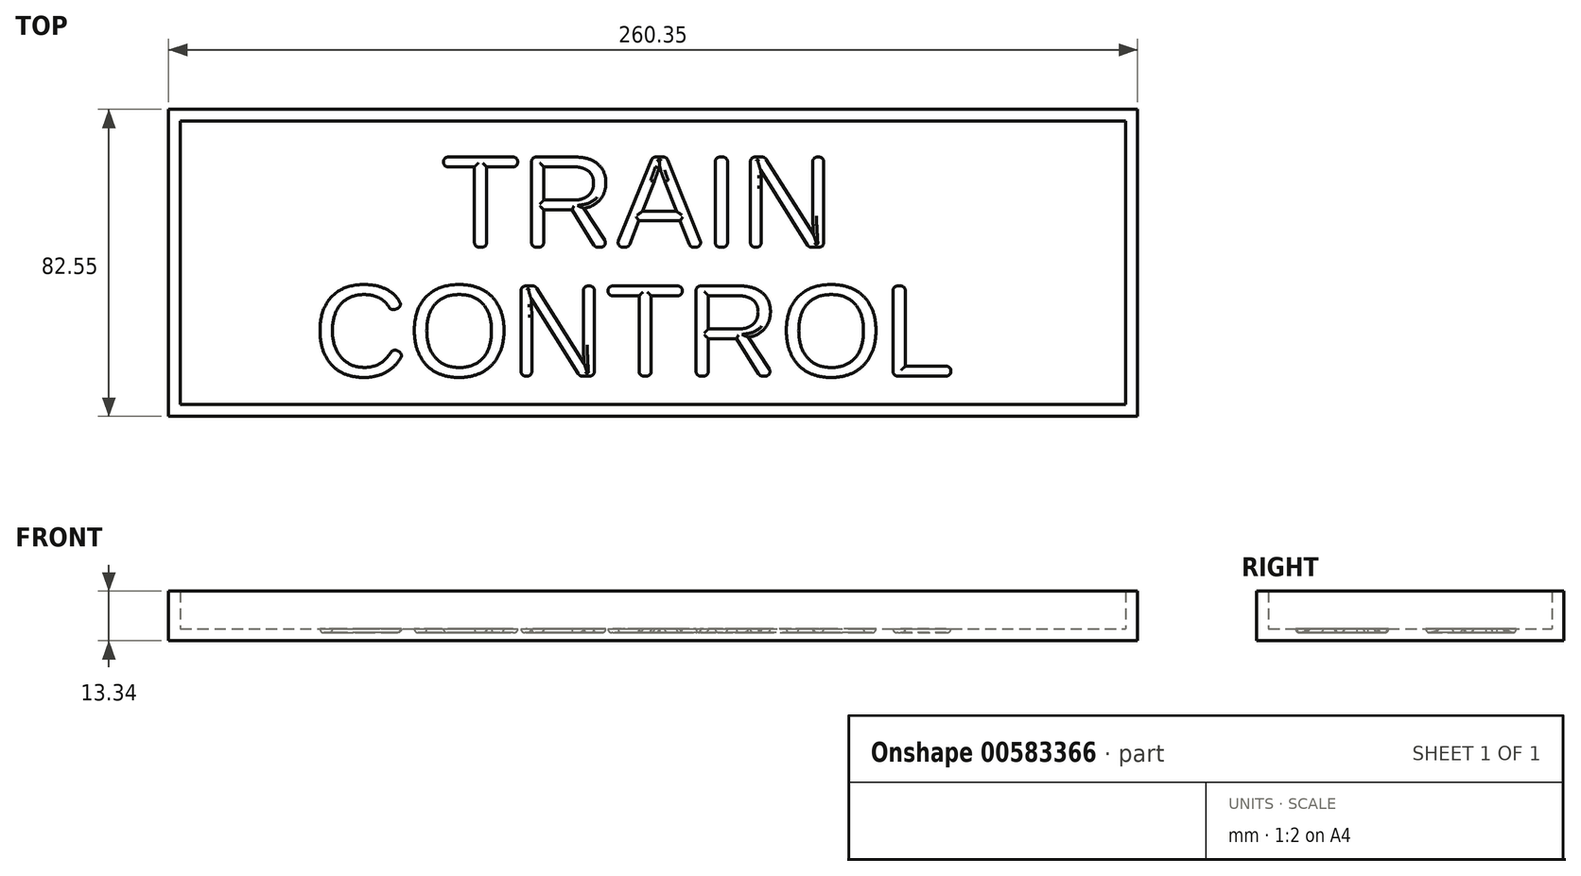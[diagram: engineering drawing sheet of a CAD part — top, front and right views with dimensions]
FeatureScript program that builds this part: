
annotation { "Feature Type Name" : "Feature", "Feature Type Description" : "" }
export const myFeature = defineFeature(function(context is Context, id is Id, definition is map)
    precondition{}
    {
        {
            var Q0;
            Q0=qCreatedBy(makeId("Top.planeOp"),FACE);
            var sketch = newSketch(context, id + "F0", { "sketchPlane" : qUnion([Q0])});
            skLineSegment(sketch, "E0.bottom", {"start": v(-122.6, -37.62) * mm, "end": v(131.4, -37.62) * mm});
            skLineSegment(sketch, "E0.top", {"start": v(-122.6, 38.58) * mm, "end": v(131.4, 38.58) * mm});
            skLineSegment(sketch, "E0.left", {"start": v(-122.6, -37.62) * mm, "end": v(-122.6, 38.58) * mm});
            skLineSegment(sketch, "E0.right", {"start": v(131.4, -37.62) * mm, "end": v(131.4, 38.58) * mm});
            skLineSegment(sketch, "E1.0", {"start": v(-125.77, 41.75) * mm, "end": v(134.58, 41.75) * mm});
            skLineSegment(sketch, "E1.1", {"start": v(-125.77, -40.8) * mm, "end": v(-125.77, 41.75) * mm});
            skLineSegment(sketch, "E1.2", {"start": v(-125.77, -40.8) * mm, "end": v(134.58, -40.8) * mm});
            skLineSegment(sketch, "E1.3", {"start": v(134.58, -40.8) * mm, "end": v(134.58, 41.75) * mm});
            skSolve(sketch);
        }
        {
            var Q0;
            Q0 = qSketchRegion(id + "F0", true);
            extrude(context, id + "F1", {"entities" : qUnion([Q0]), "depth" : 10.16 * mm, "offsetDistance" : 25.4 * mm});
        }
        {
            var Q0;
            Q0=qCreatedBy(makeId("Top.planeOp"),FACE);
            var sketch = newSketch(context, id + "F2", { "sketchPlane" : qUnion([Q0])});
            skLineSegment(sketch, "E2.0", {"start": v(-125.77, -40.8) * mm, "end": v(-125.77, 41.75) * mm});
            skLineSegment(sketch, "E2.1.0", {"start": v(134.58, -40.8) * mm, "end": v(-125.77, -40.8) * mm});
            skLineSegment(sketch, "E2.1.1", {"start": v(-125.77, -40.8) * mm, "end": v(-125.77, 41.75) * mm});
            skLineSegment(sketch, "E2.1.2", {"start": v(-125.77, 41.75) * mm, "end": v(134.58, 41.75) * mm});
            skLineSegment(sketch, "E2.1.3", {"start": v(134.58, 41.75) * mm, "end": v(134.58, -40.8) * mm});
            skSolve(sketch);
        }
        {
            var Q0;
            Q0 = qSketchRegion(id + "F2", true);
            extrude(context, id + "F3", {"entities" : qUnion([Q0]), "operationType" : NewBodyOperationType.ADD, "oppositeDirection" : true, "depth" : 3.17 * mm, "offsetDistance" : 25.4 * mm});
        }
        {
            var Q0;
            Q0=makeQuery(id+"F3.opExtrude","CAP_FACE",FACE,{"disambiguationData":[OSD([sQuery(id+"F2.wireOp",EDGE,"E2.1.0"),sQuery(id+"F2.wireOp",EDGE,"E2.1.1"),sQuery(id+"F2.wireOp",EDGE,"E2.1.2"),sQuery(id+"F2.wireOp",EDGE,"E2.1.3")])],"isStart":true});
            var sketch = newSketch(context, id + "F4", { "sketchPlane" : qUnion([Q0])});
            skText(sketch, "E3", { "text": "TRAIN", "fontName": "Arimo-Regular.ttf"});
            skText(sketch, "E4", { "text": "CONTROL", "fontName": "Arimo-Regular.ttf"});
            const initialGuessF4  = {"E3": [-0.0527, 0.00468, 1, 0, 0.0254], "E4": [-0.08688, -0.02998, 1, 0, 0.0254]};
            skSetInitialGuess(sketch, initialGuessF4);
            skSolve(sketch);
        }
        {
            var Q0;
            Q0 = qSketchRegion(id + "F4", true);
            extrude(context, id + "F5", {"entities" : qUnion([Q0]), "operationType" : NewBodyOperationType.REMOVE, "oppositeDirection" : true, "depth" : 1.02 * mm, "offsetDistance" : 25.4 * mm});
        }
        {
            var Q0;
            Q0=makeQuery(id+"F5.boolean.opBoolean","COPY",EDGE,{"derivedFrom":makeQuery(id+"F5.opExtrude","SWEPT_EDGE",EDGE,{"disambiguationData":[OSD([sQuery(id+"F4.wireOp",EDGE,"E3.sketch_text.stroke-4"),sQuery(id+"F4.wireOp",EDGE,"E3.sketch_text.stroke-5")])]})});
            var Q1;
            Q1=makeQuery(id+"F5.boolean.opBoolean","COPY",EDGE,{"derivedFrom":makeQuery(id+"F5.opExtrude","SWEPT_EDGE",EDGE,{"disambiguationData":[OSD([sQuery(id+"F4.wireOp",EDGE,"E3.sketch_text.stroke-5"),sQuery(id+"F4.wireOp",EDGE,"E3.sketch_text.stroke-6")])]})});
            var Q2;
            Q2=makeQuery(id+"F5.boolean.opBoolean","COPY",EDGE,{"derivedFrom":makeQuery(id+"F5.opExtrude","SWEPT_EDGE",EDGE,{"disambiguationData":[OSD([sQuery(id+"F4.wireOp",EDGE,"E3.sketch_text.stroke-6"),sQuery(id+"F4.wireOp",EDGE,"E3.sketch_text.stroke-7")])]})});
            var Q3;
            Q3=makeQuery(id+"F5.boolean.opBoolean","COPY",EDGE,{"derivedFrom":makeQuery(id+"F5.opExtrude","SWEPT_EDGE",EDGE,{"disambiguationData":[OSD([sQuery(id+"F4.wireOp",EDGE,"E3.sketch_text.stroke-3"),sQuery(id+"F4.wireOp",EDGE,"E3.sketch_text.stroke-4")])]})});
            var Q4;
            Q4=makeQuery(id+"F5.boolean.opBoolean","COPY",EDGE,{"derivedFrom":makeQuery(id+"F5.opExtrude","SWEPT_EDGE",EDGE,{"disambiguationData":[OSD([sQuery(id+"F4.wireOp",EDGE,"E3.sketch_text.stroke-1"),sQuery(id+"F4.wireOp",EDGE,"E3.sketch_text.stroke-2")])]})});
            var Q5;
            Q5=makeQuery(id+"F5.boolean.opBoolean","COPY",EDGE,{"derivedFrom":makeQuery(id+"F5.opExtrude","SWEPT_EDGE",EDGE,{"disambiguationData":[OSD([sQuery(id+"F4.wireOp",EDGE,"E3.sketch_text.stroke-11"),sQuery(id+"F4.wireOp",EDGE,"E3.sketch_text.stroke-12")])]})});
            var Q6;
            Q6=makeQuery(id+"F5.boolean.opBoolean","COPY",EDGE,{"derivedFrom":makeQuery(id+"F5.opExtrude","SWEPT_EDGE",EDGE,{"disambiguationData":[OSD([sQuery(id+"F4.wireOp",EDGE,"E3.sketch_text.stroke-8"),sQuery(id+"F4.wireOp",EDGE,"E3.sketch_text.stroke-19")])]})});
            var Q7;
            Q7=makeQuery(id+"F5.boolean.opBoolean","COPY",EDGE,{"derivedFrom":makeQuery(id+"F5.opExtrude","SWEPT_EDGE",EDGE,{"disambiguationData":[OSD([sQuery(id+"F4.wireOp",EDGE,"E3.sketch_text.stroke-30"),sQuery(id+"F4.wireOp",EDGE,"E3.sketch_text.stroke-31")])]})});
            var Q8;
            Q8=makeQuery(id+"F5.boolean.opBoolean","COPY",EDGE,{"derivedFrom":makeQuery(id+"F5.opExtrude","SWEPT_EDGE",EDGE,{"disambiguationData":[OSD([sQuery(id+"F4.wireOp",EDGE,"E3.sketch_text.stroke-27"),sQuery(id+"F4.wireOp",EDGE,"E3.sketch_text.stroke-34")])]})});
            var Q9;
            Q9=makeQuery(id+"F5.boolean.opBoolean","COPY",EDGE,{"derivedFrom":makeQuery(id+"F5.opExtrude","SWEPT_EDGE",EDGE,{"disambiguationData":[OSD([sQuery(id+"F4.wireOp",EDGE,"E3.sketch_text.stroke-42"),sQuery(id+"F4.wireOp",EDGE,"E3.sketch_text.stroke-45")])]})});
            var Q10;
            Q10=makeQuery(id+"F5.boolean.opBoolean","COPY",EDGE,{"derivedFrom":makeQuery(id+"F5.opExtrude","SWEPT_EDGE",EDGE,{"disambiguationData":[OSD([sQuery(id+"F4.wireOp",EDGE,"E3.sketch_text.stroke-50"),sQuery(id+"F4.wireOp",EDGE,"E3.sketch_text.stroke-51")])]})});
            var Q11;
            Q11=makeQuery(id+"F5.boolean.opBoolean","COPY",EDGE,{"derivedFrom":makeQuery(id+"F5.opExtrude","SWEPT_EDGE",EDGE,{"disambiguationData":[OSD([sQuery(id+"F4.wireOp",EDGE,"E3.sketch_text.stroke-46"),sQuery(id+"F4.wireOp",EDGE,"E3.sketch_text.stroke-58")])]})});
            var Q12;
            Q12=makeQuery(id+"F5.boolean.opBoolean","COPY",EDGE,{"derivedFrom":makeQuery(id+"F5.opExtrude","SWEPT_EDGE",EDGE,{"disambiguationData":[OSD([sQuery(id+"F4.wireOp",EDGE,"E4.sketch_text.stroke-15"),sQuery(id+"F4.wireOp",EDGE,"E4.sketch_text.stroke-16")])]})});
            var Q13;
            Q13=makeQuery(id+"F5.boolean.opBoolean","COPY",EDGE,{"derivedFrom":makeQuery(id+"F5.opExtrude","SWEPT_EDGE",EDGE,{"disambiguationData":[OSD([sQuery(id+"F4.wireOp",EDGE,"E4.sketch_text.stroke-41"),sQuery(id+"F4.wireOp",EDGE,"E4.sketch_text.stroke-42")])]})});
            var Q14;
            Q14=makeQuery(id+"F5.boolean.opBoolean","COPY",EDGE,{"derivedFrom":makeQuery(id+"F5.opExtrude","SWEPT_EDGE",EDGE,{"disambiguationData":[OSD([sQuery(id+"F4.wireOp",EDGE,"E4.sketch_text.stroke-37"),sQuery(id+"F4.wireOp",EDGE,"E4.sketch_text.stroke-49")])]})});
            var Q15;
            Q15=makeQuery(id+"F5.boolean.opBoolean","COPY",EDGE,{"derivedFrom":makeQuery(id+"F5.opExtrude","SWEPT_EDGE",EDGE,{"disambiguationData":[OSD([sQuery(id+"F4.wireOp",EDGE,"E4.sketch_text.stroke-51"),sQuery(id+"F4.wireOp",EDGE,"E4.sketch_text.stroke-52")])]})});
            var Q16;
            Q16=makeQuery(id+"F5.boolean.opBoolean","COPY",EDGE,{"derivedFrom":makeQuery(id+"F5.opExtrude","SWEPT_EDGE",EDGE,{"disambiguationData":[OSD([sQuery(id+"F4.wireOp",EDGE,"E4.sketch_text.stroke-53"),sQuery(id+"F4.wireOp",EDGE,"E4.sketch_text.stroke-54")])]})});
            var Q17;
            Q17=makeQuery(id+"F5.boolean.opBoolean","COPY",EDGE,{"derivedFrom":makeQuery(id+"F5.opExtrude","SWEPT_EDGE",EDGE,{"disambiguationData":[OSD([sQuery(id+"F4.wireOp",EDGE,"E4.sketch_text.stroke-61"),sQuery(id+"F4.wireOp",EDGE,"E4.sketch_text.stroke-62")])]})});
            var Q18;
            Q18=makeQuery(id+"F5.boolean.opBoolean","COPY",EDGE,{"derivedFrom":makeQuery(id+"F5.opExtrude","SWEPT_EDGE",EDGE,{"disambiguationData":[OSD([sQuery(id+"F4.wireOp",EDGE,"E4.sketch_text.stroke-58"),sQuery(id+"F4.wireOp",EDGE,"E4.sketch_text.stroke-69")])]})});
            var Q19;
            Q19=makeQuery(id+"F5.boolean.opBoolean","COPY",EDGE,{"derivedFrom":makeQuery(id+"F5.opExtrude","SWEPT_EDGE",EDGE,{"disambiguationData":[OSD([sQuery(id+"F4.wireOp",EDGE,"E4.sketch_text.stroke-68"),sQuery(id+"F4.wireOp",EDGE,"E4.sketch_text.stroke-69")])]})});
            var Q20;
            Q20=makeQuery(id+"F5.boolean.opBoolean","COPY",EDGE,{"derivedFrom":makeQuery(id+"F5.opExtrude","SWEPT_EDGE",EDGE,{"disambiguationData":[OSD([sQuery(id+"F4.wireOp",EDGE,"E4.sketch_text.stroke-60"),sQuery(id+"F4.wireOp",EDGE,"E4.sketch_text.stroke-61")])]})});
            var Q21;
            Q21=makeQuery(id+"F5.boolean.opBoolean","COPY",EDGE,{"derivedFrom":makeQuery(id+"F5.opExtrude","SWEPT_EDGE",EDGE,{"disambiguationData":[OSD([sQuery(id+"F4.wireOp",EDGE,"E4.sketch_text.stroke-50"),sQuery(id+"F4.wireOp",EDGE,"E4.sketch_text.stroke-51")])]})});
            var Q22;
            Q22=makeQuery(id+"F5.boolean.opBoolean","COPY",EDGE,{"derivedFrom":makeQuery(id+"F5.opExtrude","SWEPT_EDGE",EDGE,{"disambiguationData":[OSD([sQuery(id+"F4.wireOp",EDGE,"E4.sketch_text.stroke-48"),sQuery(id+"F4.wireOp",EDGE,"E4.sketch_text.stroke-49")])]})});
            var Q23;
            Q23=makeQuery(id+"F5.boolean.opBoolean","COPY",EDGE,{"derivedFrom":makeQuery(id+"F5.opExtrude","SWEPT_EDGE",EDGE,{"disambiguationData":[OSD([sQuery(id+"F4.wireOp",EDGE,"E4.sketch_text.stroke-14"),sQuery(id+"F4.wireOp",EDGE,"E4.sketch_text.stroke-15")])]})});
            var Q24;
            Q24=makeQuery(id+"F5.boolean.opBoolean","COPY",EDGE,{"derivedFrom":makeQuery(id+"F5.opExtrude","SWEPT_EDGE",EDGE,{"disambiguationData":[OSD([sQuery(id+"F4.wireOp",EDGE,"E4.sketch_text.stroke-4"),sQuery(id+"F4.wireOp",EDGE,"E4.sketch_text.stroke-5")])]})});
            var Q25;
            Q25=makeQuery(id+"F5.boolean.opBoolean","COPY",EDGE,{"derivedFrom":makeQuery(id+"F5.opExtrude","SWEPT_EDGE",EDGE,{"disambiguationData":[OSD([sQuery(id+"F4.wireOp",EDGE,"E4.sketch_text.stroke-5"),sQuery(id+"F4.wireOp",EDGE,"E4.sketch_text.stroke-6")])]})});
            var Q26;
            Q26=makeQuery(id+"F5.boolean.opBoolean","COPY",EDGE,{"derivedFrom":makeQuery(id+"F5.opExtrude","SWEPT_EDGE",EDGE,{"disambiguationData":[OSD([sQuery(id+"F4.wireOp",EDGE,"E4.sketch_text.stroke-40"),sQuery(id+"F4.wireOp",EDGE,"E4.sketch_text.stroke-41")])]})});
            var Q27;
            Q27=makeQuery(id+"F5.boolean.opBoolean","COPY",EDGE,{"derivedFrom":makeQuery(id+"F5.opExtrude","SWEPT_EDGE",EDGE,{"disambiguationData":[OSD([sQuery(id+"F4.wireOp",EDGE,"E4.sketch_text.stroke-56"),sQuery(id+"F4.wireOp",EDGE,"E4.sketch_text.stroke-57")])]})});
            var Q28;
            Q28=makeQuery(id+"F5.boolean.opBoolean","COPY",EDGE,{"derivedFrom":makeQuery(id+"F5.opExtrude","SWEPT_EDGE",EDGE,{"disambiguationData":[OSD([sQuery(id+"F4.wireOp",EDGE,"E4.sketch_text.stroke-46"),sQuery(id+"F4.wireOp",EDGE,"E4.sketch_text.stroke-47")])]})});
            var Q29;
            Q29=makeQuery(id+"F5.boolean.opBoolean","COPY",EDGE,{"derivedFrom":makeQuery(id+"F5.opExtrude","SWEPT_EDGE",EDGE,{"disambiguationData":[OSD([sQuery(id+"F4.wireOp",EDGE,"E4.sketch_text.stroke-54"),sQuery(id+"F4.wireOp",EDGE,"E4.sketch_text.stroke-55")])]})});
            var Q30;
            Q30=makeQuery(id+"F5.boolean.opBoolean","COPY",EDGE,{"derivedFrom":makeQuery(id+"F5.opExtrude","SWEPT_EDGE",EDGE,{"disambiguationData":[OSD([sQuery(id+"F4.wireOp",EDGE,"E4.sketch_text.stroke-55"),sQuery(id+"F4.wireOp",EDGE,"E4.sketch_text.stroke-56")])]})});
            var Q31;
            Q31=makeQuery(id+"F5.boolean.opBoolean","COPY",EDGE,{"derivedFrom":makeQuery(id+"F5.opExtrude","SWEPT_EDGE",EDGE,{"disambiguationData":[OSD([sQuery(id+"F4.wireOp",EDGE,"E4.sketch_text.stroke-47"),sQuery(id+"F4.wireOp",EDGE,"E4.sketch_text.stroke-48")])]})});
            var Q32;
            Q32=makeQuery(id+"F5.boolean.opBoolean","COPY",EDGE,{"derivedFrom":makeQuery(id+"F5.opExtrude","SWEPT_EDGE",EDGE,{"disambiguationData":[OSD([sQuery(id+"F4.wireOp",EDGE,"E4.sketch_text.stroke-43"),sQuery(id+"F4.wireOp",EDGE,"E4.sketch_text.stroke-44")])]})});
            var Q33;
            Q33=makeQuery(id+"F5.boolean.opBoolean","COPY",EDGE,{"derivedFrom":makeQuery(id+"F5.opExtrude","SWEPT_EDGE",EDGE,{"disambiguationData":[OSD([sQuery(id+"F4.wireOp",EDGE,"E4.sketch_text.stroke-42"),sQuery(id+"F4.wireOp",EDGE,"E4.sketch_text.stroke-43")])]})});
            var Q34;
            Q34=makeQuery(id+"F5.boolean.opBoolean","COPY",EDGE,{"derivedFrom":makeQuery(id+"F5.opExtrude","SWEPT_EDGE",EDGE,{"disambiguationData":[OSD([sQuery(id+"F4.wireOp",EDGE,"E3.sketch_text.stroke-12"),sQuery(id+"F4.wireOp",EDGE,"E3.sketch_text.stroke-13")])]})});
            var Q35;
            Q35=makeQuery(id+"F5.boolean.opBoolean","COPY",EDGE,{"derivedFrom":makeQuery(id+"F5.opExtrude","SWEPT_EDGE",EDGE,{"disambiguationData":[OSD([sQuery(id+"F4.wireOp",EDGE,"E3.sketch_text.stroke-0"),sQuery(id+"F4.wireOp",EDGE,"E3.sketch_text.stroke-1")])]})});
            var Q36;
            Q36=makeQuery(id+"F5.boolean.opBoolean","COPY",EDGE,{"derivedFrom":makeQuery(id+"F5.opExtrude","SWEPT_EDGE",EDGE,{"disambiguationData":[OSD([sQuery(id+"F4.wireOp",EDGE,"E3.sketch_text.stroke-10"),sQuery(id+"F4.wireOp",EDGE,"E3.sketch_text.stroke-11")])]})});
            var Q37;
            Q37=makeQuery(id+"F5.boolean.opBoolean","COPY",EDGE,{"derivedFrom":makeQuery(id+"F5.opExtrude","SWEPT_EDGE",EDGE,{"disambiguationData":[OSD([sQuery(id+"F4.wireOp",EDGE,"E3.sketch_text.stroke-18"),sQuery(id+"F4.wireOp",EDGE,"E3.sketch_text.stroke-19")])]})});
            var Q38;
            Q38=makeQuery(id+"F5.boolean.opBoolean","COPY",EDGE,{"derivedFrom":makeQuery(id+"F5.opExtrude","SWEPT_EDGE",EDGE,{"disambiguationData":[OSD([sQuery(id+"F4.wireOp",EDGE,"E3.sketch_text.stroke-29"),sQuery(id+"F4.wireOp",EDGE,"E3.sketch_text.stroke-30")])]})});
            var Q39;
            Q39=makeQuery(id+"F5.boolean.opBoolean","COPY",EDGE,{"derivedFrom":makeQuery(id+"F5.opExtrude","SWEPT_EDGE",EDGE,{"disambiguationData":[OSD([sQuery(id+"F4.wireOp",EDGE,"E3.sketch_text.stroke-33"),sQuery(id+"F4.wireOp",EDGE,"E3.sketch_text.stroke-34")])]})});
            var Q40;
            Q40=makeQuery(id+"F5.boolean.opBoolean","COPY",EDGE,{"derivedFrom":makeQuery(id+"F5.opExtrude","SWEPT_EDGE",EDGE,{"disambiguationData":[OSD([sQuery(id+"F4.wireOp",EDGE,"E3.sketch_text.stroke-44"),sQuery(id+"F4.wireOp",EDGE,"E3.sketch_text.stroke-45")])]})});
            var Q41;
            Q41=makeQuery(id+"F5.boolean.opBoolean","COPY",EDGE,{"derivedFrom":makeQuery(id+"F5.opExtrude","SWEPT_EDGE",EDGE,{"disambiguationData":[OSD([sQuery(id+"F4.wireOp",EDGE,"E3.sketch_text.stroke-49"),sQuery(id+"F4.wireOp",EDGE,"E3.sketch_text.stroke-50")])]})});
            var Q42;
            Q42=makeQuery(id+"F5.boolean.opBoolean","COPY",EDGE,{"derivedFrom":makeQuery(id+"F5.opExtrude","SWEPT_EDGE",EDGE,{"disambiguationData":[OSD([sQuery(id+"F4.wireOp",EDGE,"E3.sketch_text.stroke-57"),sQuery(id+"F4.wireOp",EDGE,"E3.sketch_text.stroke-58")])]})});
            var Q43;
            Q43=makeQuery(id+"F5.boolean.opBoolean","COPY",EDGE,{"derivedFrom":makeQuery(id+"F5.opExtrude","SWEPT_EDGE",EDGE,{"disambiguationData":[OSD([sQuery(id+"F4.wireOp",EDGE,"E4.sketch_text.stroke-100"),sQuery(id+"F4.wireOp",EDGE,"E4.sketch_text.stroke-101")])]})});
            var Q44;
            Q44=makeQuery(id+"F5.boolean.opBoolean","COPY",EDGE,{"derivedFrom":makeQuery(id+"F5.opExtrude","SWEPT_EDGE",EDGE,{"disambiguationData":[OSD([sQuery(id+"F4.wireOp",EDGE,"E4.sketch_text.stroke-62"),sQuery(id+"F4.wireOp",EDGE,"E4.sketch_text.stroke-63")])]})});
            var Q45;
            Q45=makeQuery(id+"F5.boolean.opBoolean","COPY",EDGE,{"derivedFrom":makeQuery(id+"F5.opExtrude","SWEPT_EDGE",EDGE,{"disambiguationData":[OSD([sQuery(id+"F4.wireOp",EDGE,"E4.sketch_text.stroke-96"),sQuery(id+"F4.wireOp",EDGE,"E4.sketch_text.stroke-97")])]})});
            var Q46;
            Q46=makeQuery(id+"F5.boolean.opBoolean","COPY",EDGE,{"derivedFrom":makeQuery(id+"F5.opExtrude","SWEPT_EDGE",EDGE,{"disambiguationData":[OSD([sQuery(id+"F4.wireOp",EDGE,"E4.sketch_text.stroke-97"),sQuery(id+"F4.wireOp",EDGE,"E4.sketch_text.stroke-98")])]})});
            var Q47;
            Q47=makeQuery(id+"F5.boolean.opBoolean","COPY",EDGE,{"derivedFrom":makeQuery(id+"F5.opExtrude","SWEPT_EDGE",EDGE,{"disambiguationData":[OSD([sQuery(id+"F4.wireOp",EDGE,"E4.sketch_text.stroke-96"),sQuery(id+"F4.wireOp",EDGE,"E4.sketch_text.stroke-101")])]})});
            var Q48;
            Q48=makeQuery(id+"F5.boolean.opBoolean","COPY",EDGE,{"derivedFrom":makeQuery(id+"F5.opExtrude","SWEPT_EDGE",EDGE,{"disambiguationData":[OSD([sQuery(id+"F4.wireOp",EDGE,"E3.sketch_text.stroke-32"),sQuery(id+"F4.wireOp",EDGE,"E3.sketch_text.stroke-33")])]})});
            var Q49;
            Q49=makeQuery(id+"F5.boolean.opBoolean","COPY",EDGE,{"derivedFrom":makeQuery(id+"F5.opExtrude","SWEPT_EDGE",EDGE,{"disambiguationData":[OSD([sQuery(id+"F4.wireOp",EDGE,"E3.sketch_text.stroke-43"),sQuery(id+"F4.wireOp",EDGE,"E3.sketch_text.stroke-44")])]})});
            var Q50;
            Q50=makeQuery(id+"F5.boolean.opBoolean","COPY",EDGE,{"derivedFrom":makeQuery(id+"F5.opExtrude","SWEPT_EDGE",EDGE,{"disambiguationData":[OSD([sQuery(id+"F4.wireOp",EDGE,"E3.sketch_text.stroke-52"),sQuery(id+"F4.wireOp",EDGE,"E3.sketch_text.stroke-53")])]})});
            var Q51;
            Q51=makeQuery(id+"F5.boolean.opBoolean","COPY",EDGE,{"derivedFrom":makeQuery(id+"F5.opExtrude","SWEPT_EDGE",EDGE,{"disambiguationData":[OSD([sQuery(id+"F4.wireOp",EDGE,"E3.sketch_text.stroke-56"),sQuery(id+"F4.wireOp",EDGE,"E3.sketch_text.stroke-57")])]})});
            var Q52;
            Q52=makeQuery(id+"F5.boolean.opBoolean","COPY",EDGE,{"derivedFrom":makeQuery(id+"F5.opExtrude","SWEPT_EDGE",EDGE,{"disambiguationData":[OSD([sQuery(id+"F4.wireOp",EDGE,"E3.sketch_text.stroke-31"),sQuery(id+"F4.wireOp",EDGE,"E3.sketch_text.stroke-32")])]})});
            var Q53;
            Q53=makeQuery(id+"F5.boolean.opBoolean","COPY",EDGE,{"derivedFrom":makeQuery(id+"F5.opExtrude","SWEPT_EDGE",EDGE,{"disambiguationData":[OSD([sQuery(id+"F4.wireOp",EDGE,"E3.sketch_text.stroke-42"),sQuery(id+"F4.wireOp",EDGE,"E3.sketch_text.stroke-43")])]})});
            var Q54;
            Q54=makeQuery(id+"F5.boolean.opBoolean","COPY",EDGE,{"derivedFrom":makeQuery(id+"F5.opExtrude","SWEPT_EDGE",EDGE,{"disambiguationData":[OSD([sQuery(id+"F4.wireOp",EDGE,"E3.sketch_text.stroke-51"),sQuery(id+"F4.wireOp",EDGE,"E3.sketch_text.stroke-52")])]})});
            var Q55;
            Q55=makeQuery(id+"F5.boolean.opBoolean","COPY",EDGE,{"derivedFrom":makeQuery(id+"F5.opExtrude","SWEPT_EDGE",EDGE,{"disambiguationData":[OSD([sQuery(id+"F4.wireOp",EDGE,"E3.sketch_text.stroke-55"),sQuery(id+"F4.wireOp",EDGE,"E3.sketch_text.stroke-56")])]})});
            var Q56;
            Q56=makeQuery(id+"F5.boolean.opBoolean","COPY",EDGE,{"derivedFrom":makeQuery(id+"F5.opExtrude","SWEPT_EDGE",EDGE,{"disambiguationData":[OSD([sQuery(id+"F4.wireOp",EDGE,"E4.sketch_text.stroke-99"),sQuery(id+"F4.wireOp",EDGE,"E4.sketch_text.stroke-100")])]})});
            fillet(context, id + "F6", {"entities" : qUnion([Q0, Q1, Q2, Q3, Q4, Q5, Q6, Q7, Q8, Q9, Q10, Q11, Q12, Q13, Q14, Q15, Q16, Q17, Q18, Q19, Q20, Q21, Q22, Q23, Q24, Q25, Q26, Q27, Q28, Q29, Q30, Q31, Q32, Q33, Q34, Q35, Q36, Q37, Q38, Q39, Q40, Q41, Q42, Q43, Q44, Q45, Q46, Q47, Q48, Q49, Q50, Q51, Q52, Q53, Q54, Q55, Q56]), "radius" : 1.27 * mm, "tangentPropagation" : true, "allowEdgeOverflow" : false});
        }
        {
            var Q0;
            Q0=makeQuery(id+"F5.boolean.opBoolean","COPY",FACE,{"derivedFrom":makeQuery(id+"F5.opExtrude","CAP_FACE",FACE,{"disambiguationData":[OSD([sQuery(id+"F4.wireOp",EDGE,"E3.sketch_text.stroke-0"),sQuery(id+"F4.wireOp",EDGE,"E3.sketch_text.stroke-1"),sQuery(id+"F4.wireOp",EDGE,"E3.sketch_text.stroke-2"),sQuery(id+"F4.wireOp",EDGE,"E3.sketch_text.stroke-3"),sQuery(id+"F4.wireOp",EDGE,"E3.sketch_text.stroke-4"),sQuery(id+"F4.wireOp",EDGE,"E3.sketch_text.stroke-5"),sQuery(id+"F4.wireOp",EDGE,"E3.sketch_text.stroke-6"),sQuery(id+"F4.wireOp",EDGE,"E3.sketch_text.stroke-7")])],"isStart":false})});
            var Q1;
            Q1=makeQuery(id+"F5.boolean.opBoolean","COPY",FACE,{"derivedFrom":makeQuery(id+"F5.opExtrude","CAP_FACE",FACE,{"disambiguationData":[OSD([sQuery(id+"F4.wireOp",EDGE,"E3.sketch_text.stroke-8"),sQuery(id+"F4.wireOp",EDGE,"E3.sketch_text.stroke-9"),sQuery(id+"F4.wireOp",EDGE,"E3.sketch_text.stroke-10"),sQuery(id+"F4.wireOp",EDGE,"E3.sketch_text.stroke-11"),sQuery(id+"F4.wireOp",EDGE,"E3.sketch_text.stroke-12"),sQuery(id+"F4.wireOp",EDGE,"E3.sketch_text.stroke-13"),sQuery(id+"F4.wireOp",EDGE,"E3.sketch_text.stroke-14"),sQuery(id+"F4.wireOp",EDGE,"E3.sketch_text.stroke-15"),sQuery(id+"F4.wireOp",EDGE,"E3.sketch_text.stroke-16"),sQuery(id+"F4.wireOp",EDGE,"E3.sketch_text.stroke-17"),sQuery(id+"F4.wireOp",EDGE,"E3.sketch_text.stroke-18"),sQuery(id+"F4.wireOp",EDGE,"E3.sketch_text.stroke-19"),sQuery(id+"F4.wireOp",EDGE,"E3.sketch_text.stroke-20"),sQuery(id+"F4.wireOp",EDGE,"E3.sketch_text.stroke-21"),sQuery(id+"F4.wireOp",EDGE,"E3.sketch_text.stroke-22"),sQuery(id+"F4.wireOp",EDGE,"E3.sketch_text.stroke-23"),sQuery(id+"F4.wireOp",EDGE,"E3.sketch_text.stroke-24"),sQuery(id+"F4.wireOp",EDGE,"E3.sketch_text.stroke-25"),sQuery(id+"F4.wireOp",EDGE,"E3.sketch_text.stroke-26")])],"isStart":false})});
            var Q2;
            Q2=makeQuery(id+"F5.boolean.opBoolean","COPY",FACE,{"derivedFrom":makeQuery(id+"F5.opExtrude","CAP_FACE",FACE,{"disambiguationData":[OSD([sQuery(id+"F4.wireOp",EDGE,"E3.sketch_text.stroke-27"),sQuery(id+"F4.wireOp",EDGE,"E3.sketch_text.stroke-28"),sQuery(id+"F4.wireOp",EDGE,"E3.sketch_text.stroke-29"),sQuery(id+"F4.wireOp",EDGE,"E3.sketch_text.stroke-30"),sQuery(id+"F4.wireOp",EDGE,"E3.sketch_text.stroke-31"),sQuery(id+"F4.wireOp",EDGE,"E3.sketch_text.stroke-32"),sQuery(id+"F4.wireOp",EDGE,"E3.sketch_text.stroke-33"),sQuery(id+"F4.wireOp",EDGE,"E3.sketch_text.stroke-34"),sQuery(id+"F4.wireOp",EDGE,"E3.sketch_text.stroke-35"),sQuery(id+"F4.wireOp",EDGE,"E3.sketch_text.stroke-36"),sQuery(id+"F4.wireOp",EDGE,"E3.sketch_text.stroke-37"),sQuery(id+"F4.wireOp",EDGE,"E3.sketch_text.stroke-38"),sQuery(id+"F4.wireOp",EDGE,"E3.sketch_text.stroke-39"),sQuery(id+"F4.wireOp",EDGE,"E3.sketch_text.stroke-40"),sQuery(id+"F4.wireOp",EDGE,"E3.sketch_text.stroke-41")])],"isStart":false})});
            var Q3;
            Q3=makeQuery(id+"F5.boolean.opBoolean","COPY",FACE,{"derivedFrom":makeQuery(id+"F5.opExtrude","CAP_FACE",FACE,{"disambiguationData":[OSD([sQuery(id+"F4.wireOp",EDGE,"E3.sketch_text.stroke-42"),sQuery(id+"F4.wireOp",EDGE,"E3.sketch_text.stroke-43"),sQuery(id+"F4.wireOp",EDGE,"E3.sketch_text.stroke-44"),sQuery(id+"F4.wireOp",EDGE,"E3.sketch_text.stroke-45")])],"isStart":false})});
            var Q4;
            Q4=makeQuery(id+"F5.boolean.opBoolean","COPY",FACE,{"derivedFrom":makeQuery(id+"F5.opExtrude","CAP_FACE",FACE,{"disambiguationData":[OSD([sQuery(id+"F4.wireOp",EDGE,"E3.sketch_text.stroke-46"),sQuery(id+"F4.wireOp",EDGE,"E3.sketch_text.stroke-47"),sQuery(id+"F4.wireOp",EDGE,"E3.sketch_text.stroke-48"),sQuery(id+"F4.wireOp",EDGE,"E3.sketch_text.stroke-49"),sQuery(id+"F4.wireOp",EDGE,"E3.sketch_text.stroke-50"),sQuery(id+"F4.wireOp",EDGE,"E3.sketch_text.stroke-51"),sQuery(id+"F4.wireOp",EDGE,"E3.sketch_text.stroke-52"),sQuery(id+"F4.wireOp",EDGE,"E3.sketch_text.stroke-53"),sQuery(id+"F4.wireOp",EDGE,"E3.sketch_text.stroke-54"),sQuery(id+"F4.wireOp",EDGE,"E3.sketch_text.stroke-55"),sQuery(id+"F4.wireOp",EDGE,"E3.sketch_text.stroke-56"),sQuery(id+"F4.wireOp",EDGE,"E3.sketch_text.stroke-57"),sQuery(id+"F4.wireOp",EDGE,"E3.sketch_text.stroke-58")])],"isStart":false})});
            var Q5;
            Q5=makeQuery(id+"F5.boolean.opBoolean","COPY",FACE,{"derivedFrom":makeQuery(id+"F5.opExtrude","CAP_FACE",FACE,{"disambiguationData":[OSD([sQuery(id+"F4.wireOp",EDGE,"E4.sketch_text.stroke-58"),sQuery(id+"F4.wireOp",EDGE,"E4.sketch_text.stroke-59"),sQuery(id+"F4.wireOp",EDGE,"E4.sketch_text.stroke-60"),sQuery(id+"F4.wireOp",EDGE,"E4.sketch_text.stroke-61"),sQuery(id+"F4.wireOp",EDGE,"E4.sketch_text.stroke-62"),sQuery(id+"F4.wireOp",EDGE,"E4.sketch_text.stroke-63"),sQuery(id+"F4.wireOp",EDGE,"E4.sketch_text.stroke-64"),sQuery(id+"F4.wireOp",EDGE,"E4.sketch_text.stroke-65"),sQuery(id+"F4.wireOp",EDGE,"E4.sketch_text.stroke-66"),sQuery(id+"F4.wireOp",EDGE,"E4.sketch_text.stroke-67"),sQuery(id+"F4.wireOp",EDGE,"E4.sketch_text.stroke-68"),sQuery(id+"F4.wireOp",EDGE,"E4.sketch_text.stroke-69"),sQuery(id+"F4.wireOp",EDGE,"E4.sketch_text.stroke-70"),sQuery(id+"F4.wireOp",EDGE,"E4.sketch_text.stroke-71"),sQuery(id+"F4.wireOp",EDGE,"E4.sketch_text.stroke-72"),sQuery(id+"F4.wireOp",EDGE,"E4.sketch_text.stroke-73"),sQuery(id+"F4.wireOp",EDGE,"E4.sketch_text.stroke-74"),sQuery(id+"F4.wireOp",EDGE,"E4.sketch_text.stroke-75"),sQuery(id+"F4.wireOp",EDGE,"E4.sketch_text.stroke-76")])],"isStart":false})});
            var Q6;
            Q6=makeQuery(id+"F5.boolean.opBoolean","COPY",FACE,{"derivedFrom":makeQuery(id+"F5.opExtrude","CAP_FACE",FACE,{"disambiguationData":[OSD([sQuery(id+"F4.wireOp",EDGE,"E4.sketch_text.stroke-50"),sQuery(id+"F4.wireOp",EDGE,"E4.sketch_text.stroke-51"),sQuery(id+"F4.wireOp",EDGE,"E4.sketch_text.stroke-52"),sQuery(id+"F4.wireOp",EDGE,"E4.sketch_text.stroke-53"),sQuery(id+"F4.wireOp",EDGE,"E4.sketch_text.stroke-54"),sQuery(id+"F4.wireOp",EDGE,"E4.sketch_text.stroke-55"),sQuery(id+"F4.wireOp",EDGE,"E4.sketch_text.stroke-56"),sQuery(id+"F4.wireOp",EDGE,"E4.sketch_text.stroke-57")])],"isStart":false})});
            var Q7;
            Q7=makeQuery(id+"F5.boolean.opBoolean","COPY",FACE,{"derivedFrom":makeQuery(id+"F5.opExtrude","CAP_FACE",FACE,{"disambiguationData":[OSD([sQuery(id+"F4.wireOp",EDGE,"E4.sketch_text.stroke-37"),sQuery(id+"F4.wireOp",EDGE,"E4.sketch_text.stroke-38"),sQuery(id+"F4.wireOp",EDGE,"E4.sketch_text.stroke-39"),sQuery(id+"F4.wireOp",EDGE,"E4.sketch_text.stroke-40"),sQuery(id+"F4.wireOp",EDGE,"E4.sketch_text.stroke-41"),sQuery(id+"F4.wireOp",EDGE,"E4.sketch_text.stroke-42"),sQuery(id+"F4.wireOp",EDGE,"E4.sketch_text.stroke-43"),sQuery(id+"F4.wireOp",EDGE,"E4.sketch_text.stroke-44"),sQuery(id+"F4.wireOp",EDGE,"E4.sketch_text.stroke-45"),sQuery(id+"F4.wireOp",EDGE,"E4.sketch_text.stroke-46"),sQuery(id+"F4.wireOp",EDGE,"E4.sketch_text.stroke-47"),sQuery(id+"F4.wireOp",EDGE,"E4.sketch_text.stroke-48"),sQuery(id+"F4.wireOp",EDGE,"E4.sketch_text.stroke-49")])],"isStart":false})});
            var Q8;
            Q8=makeQuery(id+"F5.boolean.opBoolean","COPY",FACE,{"derivedFrom":makeQuery(id+"F5.opExtrude","CAP_FACE",FACE,{"disambiguationData":[OSD([sQuery(id+"F4.wireOp",EDGE,"E4.sketch_text.stroke-18"),sQuery(id+"F4.wireOp",EDGE,"E4.sketch_text.stroke-19"),sQuery(id+"F4.wireOp",EDGE,"E4.sketch_text.stroke-20"),sQuery(id+"F4.wireOp",EDGE,"E4.sketch_text.stroke-21"),sQuery(id+"F4.wireOp",EDGE,"E4.sketch_text.stroke-22"),sQuery(id+"F4.wireOp",EDGE,"E4.sketch_text.stroke-23"),sQuery(id+"F4.wireOp",EDGE,"E4.sketch_text.stroke-24"),sQuery(id+"F4.wireOp",EDGE,"E4.sketch_text.stroke-25"),sQuery(id+"F4.wireOp",EDGE,"E4.sketch_text.stroke-26"),sQuery(id+"F4.wireOp",EDGE,"E4.sketch_text.stroke-27"),sQuery(id+"F4.wireOp",EDGE,"E4.sketch_text.stroke-28"),sQuery(id+"F4.wireOp",EDGE,"E4.sketch_text.stroke-29"),sQuery(id+"F4.wireOp",EDGE,"E4.sketch_text.stroke-30"),sQuery(id+"F4.wireOp",EDGE,"E4.sketch_text.stroke-31"),sQuery(id+"F4.wireOp",EDGE,"E4.sketch_text.stroke-32"),sQuery(id+"F4.wireOp",EDGE,"E4.sketch_text.stroke-33"),sQuery(id+"F4.wireOp",EDGE,"E4.sketch_text.stroke-34"),sQuery(id+"F4.wireOp",EDGE,"E4.sketch_text.stroke-35"),sQuery(id+"F4.wireOp",EDGE,"E4.sketch_text.stroke-36")])],"isStart":false})});
            var Q9;
            Q9=makeQuery(id+"F5.boolean.opBoolean","COPY",FACE,{"derivedFrom":makeQuery(id+"F5.opExtrude","CAP_FACE",FACE,{"disambiguationData":[OSD([sQuery(id+"F4.wireOp",EDGE,"E4.sketch_text.stroke-0"),sQuery(id+"F4.wireOp",EDGE,"E4.sketch_text.stroke-1"),sQuery(id+"F4.wireOp",EDGE,"E4.sketch_text.stroke-2"),sQuery(id+"F4.wireOp",EDGE,"E4.sketch_text.stroke-3"),sQuery(id+"F4.wireOp",EDGE,"E4.sketch_text.stroke-4"),sQuery(id+"F4.wireOp",EDGE,"E4.sketch_text.stroke-5"),sQuery(id+"F4.wireOp",EDGE,"E4.sketch_text.stroke-6"),sQuery(id+"F4.wireOp",EDGE,"E4.sketch_text.stroke-7"),sQuery(id+"F4.wireOp",EDGE,"E4.sketch_text.stroke-8"),sQuery(id+"F4.wireOp",EDGE,"E4.sketch_text.stroke-9"),sQuery(id+"F4.wireOp",EDGE,"E4.sketch_text.stroke-10"),sQuery(id+"F4.wireOp",EDGE,"E4.sketch_text.stroke-11"),sQuery(id+"F4.wireOp",EDGE,"E4.sketch_text.stroke-12"),sQuery(id+"F4.wireOp",EDGE,"E4.sketch_text.stroke-13"),sQuery(id+"F4.wireOp",EDGE,"E4.sketch_text.stroke-14"),sQuery(id+"F4.wireOp",EDGE,"E4.sketch_text.stroke-15"),sQuery(id+"F4.wireOp",EDGE,"E4.sketch_text.stroke-16"),sQuery(id+"F4.wireOp",EDGE,"E4.sketch_text.stroke-17")])],"isStart":false})});
            var Q10;
            Q10=makeQuery(id+"F5.boolean.opBoolean","COPY",FACE,{"derivedFrom":makeQuery(id+"F5.opExtrude","CAP_FACE",FACE,{"disambiguationData":[OSD([sQuery(id+"F4.wireOp",EDGE,"E4.sketch_text.stroke-77"),sQuery(id+"F4.wireOp",EDGE,"E4.sketch_text.stroke-78"),sQuery(id+"F4.wireOp",EDGE,"E4.sketch_text.stroke-79"),sQuery(id+"F4.wireOp",EDGE,"E4.sketch_text.stroke-80"),sQuery(id+"F4.wireOp",EDGE,"E4.sketch_text.stroke-81"),sQuery(id+"F4.wireOp",EDGE,"E4.sketch_text.stroke-82"),sQuery(id+"F4.wireOp",EDGE,"E4.sketch_text.stroke-83"),sQuery(id+"F4.wireOp",EDGE,"E4.sketch_text.stroke-84"),sQuery(id+"F4.wireOp",EDGE,"E4.sketch_text.stroke-85"),sQuery(id+"F4.wireOp",EDGE,"E4.sketch_text.stroke-86"),sQuery(id+"F4.wireOp",EDGE,"E4.sketch_text.stroke-87"),sQuery(id+"F4.wireOp",EDGE,"E4.sketch_text.stroke-88"),sQuery(id+"F4.wireOp",EDGE,"E4.sketch_text.stroke-89"),sQuery(id+"F4.wireOp",EDGE,"E4.sketch_text.stroke-90"),sQuery(id+"F4.wireOp",EDGE,"E4.sketch_text.stroke-91"),sQuery(id+"F4.wireOp",EDGE,"E4.sketch_text.stroke-92"),sQuery(id+"F4.wireOp",EDGE,"E4.sketch_text.stroke-93"),sQuery(id+"F4.wireOp",EDGE,"E4.sketch_text.stroke-94"),sQuery(id+"F4.wireOp",EDGE,"E4.sketch_text.stroke-95")])],"isStart":false})});
            var Q11;
            Q11=makeQuery(id+"F5.boolean.opBoolean","COPY",FACE,{"derivedFrom":makeQuery(id+"F5.opExtrude","CAP_FACE",FACE,{"disambiguationData":[OSD([sQuery(id+"F4.wireOp",EDGE,"E4.sketch_text.stroke-96"),sQuery(id+"F4.wireOp",EDGE,"E4.sketch_text.stroke-97"),sQuery(id+"F4.wireOp",EDGE,"E4.sketch_text.stroke-98"),sQuery(id+"F4.wireOp",EDGE,"E4.sketch_text.stroke-99"),sQuery(id+"F4.wireOp",EDGE,"E4.sketch_text.stroke-100"),sQuery(id+"F4.wireOp",EDGE,"E4.sketch_text.stroke-101")])],"isStart":false})});
            var Q12;
            Q12=makeQuery(id+"F5.boolean.opBoolean","COPY",EDGE,{"derivedFrom":makeQuery(id+"F5.opExtrude","SWEPT_EDGE",EDGE,{"disambiguationData":[OSD([sQuery(id+"F4.wireOp",EDGE,"E4.sketch_text.stroke-97"),sQuery(id+"F4.wireOp",EDGE,"E4.sketch_text.stroke-98")])]})});
            var Q13;
            Q13=makeQuery(id+"F5.boolean.opBoolean","COPY",EDGE,{"derivedFrom":makeQuery(id+"F5.opExtrude","SWEPT_EDGE",EDGE,{"disambiguationData":[OSD([sQuery(id+"F4.wireOp",EDGE,"E4.sketch_text.stroke-96"),sQuery(id+"F4.wireOp",EDGE,"E4.sketch_text.stroke-97")])]})});
            fillet(context, id + "F7", {"entities" : qUnion([Q0, Q1, Q2, Q3, Q4, Q5, Q6, Q7, Q8, Q9, Q10, Q11, Q12, Q13]), "radius" : 1.02 * mm, "tangentPropagation" : true, "allowEdgeOverflow" : false});
        }
    });
